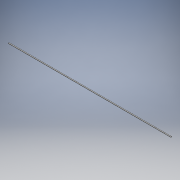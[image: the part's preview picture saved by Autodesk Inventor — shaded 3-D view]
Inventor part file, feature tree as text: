
AUTODESK INVENTOR PART (.ipt)
format: ipt  version: 2016 (Build 200138000, 138)  size: 88,576 bytes
history: native  units: in
note: dims shown in document units (in); Inventor stores cm internally (conversion verified against a paired STEP export)
features: extrude x1, sketch x1
ambient origin geometry x8: Origin, YZ Plane, XZ Plane, XY Plane, X Axis, Y Axis, Z Axis, Center Point
bodies: Solid1 (feature_tree)
feature tree (2):
  extrude  "Extrusion1"  Depth=0.125in TaperAngle=0.0deg
  sketch  "Sketch1"  dims[d0=74.0in d1=0.125in d2=0.0in]
